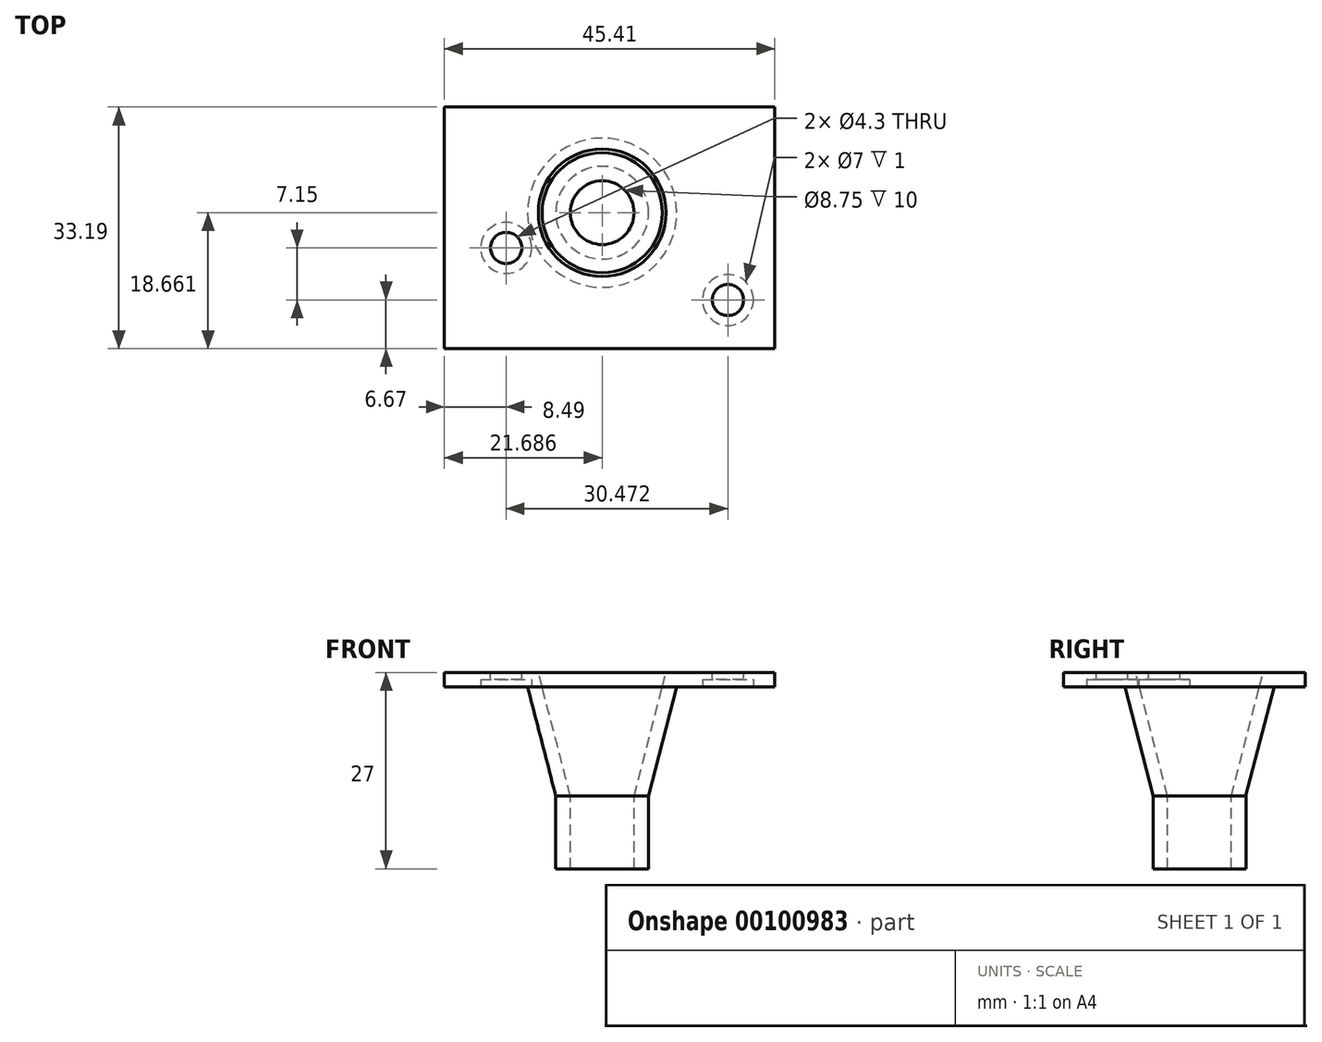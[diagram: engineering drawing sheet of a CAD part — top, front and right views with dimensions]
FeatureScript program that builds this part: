
annotation { "Feature Type Name" : "Feature", "Feature Type Description" : "" }
export const myFeature = defineFeature(function(context is Context, id is Id, definition is map)
    precondition{}
    {
        {
            var Q0;
            Q0=qCreatedBy(makeId("Top.planeOp"),FACE);
            var sketch = newSketch(context, id + "F0", { "sketchPlane" : qUnion([Q0])});
            skCircle(sketch, "E0", {"center": v(30.47, -7.15) * mm, "radius": 2.15 * mm});
            skCircle(sketch, "E1", {"center": v(0, 0) * mm, "radius": 2.15 * mm});
            skLineSegment(sketch, "E2.bottom", {"start": v(18.9, -0.85) * mm, "end": v(7.4, -0.85) * mm});
            skLineSegment(sketch, "E2.top", {"start": v(18.9, 10.65) * mm, "end": v(7.39, 10.65) * mm});
            skLineSegment(sketch, "E2.left", {"start": v(18.9, -0.85) * mm, "end": v(18.9, 10.65) * mm});
            skLineSegment(sketch, "E2.right", {"start": v(7.4, -0.85) * mm, "end": v(7.39, 10.65) * mm});
            skLineSegment(sketch, "E3.bottom", {"start": v(36.92, -13.82) * mm, "end": v(-8.49, -13.82) * mm});
            skLineSegment(sketch, "E3.top", {"start": v(36.92, 19.37) * mm, "end": v(-8.49, 19.37) * mm});
            skLineSegment(sketch, "E3.left", {"start": v(36.92, -13.82) * mm, "end": v(36.92, 19.37) * mm});
            skLineSegment(sketch, "E3.right", {"start": v(-8.49, -13.82) * mm, "end": v(-8.49, 19.37) * mm});
            skSolve(sketch);
        }
        {
            var Q0;
            Q0=makeQuery(id+"F0.imprint","IMPRINT",FACE,{"disambiguationData":[TD([[makeQuery(id+"F0.imprint","IMPRINT",EDGE,{"derivedFrom":sQuery(id+"F0.wireOp",EDGE,"E0")}),-1.0]])]});
            var Q1;
            Q1=makeQuery(id+"F0.imprint","IMPRINT",FACE,{"disambiguationData":[TD([[makeQuery(id+"F0.imprint","IMPRINT",EDGE,{"derivedFrom":sQuery(id+"F0.wireOp",EDGE,"E2.bottom")}),1.0]])]});
            extrude(context, id + "F1", {"entities" : qUnion([Q0, Q1]), "oppositeDirection" : true, "depth" : 2 * mm});
        }
        {
            var Q0;
            Q0=makeQuery(id+"F1.opExtrude","CAP_FACE",FACE,{"disambiguationData":[OSD([sQuery(id+"F0.wireOp",EDGE,"E0"),sQuery(id+"F0.wireOp",EDGE,"E1"),sQuery(id+"F0.wireOp",EDGE,"E2.bottom"),sQuery(id+"F0.wireOp",EDGE,"E2.top"),sQuery(id+"F0.wireOp",EDGE,"E2.left"),sQuery(id+"F0.wireOp",EDGE,"E2.right"),sQuery(id+"F0.wireOp",EDGE,"E3.bottom"),sQuery(id+"F0.wireOp",EDGE,"E3.top"),sQuery(id+"F0.wireOp",EDGE,"E3.left"),sQuery(id+"F0.wireOp",EDGE,"E3.right")])],"isStart":false});
            var sketch = newSketch(context, id + "F2", { "sketchPlane" : qUnion([Q0])});
            skCircle(sketch, "E4", {"center": v(0, 0) * mm, "radius": 3.5 * mm});
            skCircle(sketch, "E5", {"center": v(30.47, 7.15) * mm, "radius": 3.5 * mm});
            skSolve(sketch);
        }
        {
            var Q0;
            Q0=makeQuery(id+"F2.imprint","IMPRINT",FACE,{"disambiguationData":[TD([[makeQuery(id+"F2.imprint","IMPRINT",EDGE,{"derivedFrom":sQuery(id+"F2.wireOp",EDGE,"E5")}),1.0]])]});
            var Q1;
            Q1=makeQuery(id+"F2.imprint","IMPRINT",FACE,{"disambiguationData":[TD([[makeQuery(id+"F2.imprint","IMPRINT",EDGE,{"derivedFrom":sQuery(id+"F2.wireOp",EDGE,"E4")}),1.0]])]});
            extrude(context, id + "F3", {"entities" : qUnion([Q0, Q1]), "operationType" : NewBodyOperationType.REMOVE, "oppositeDirection" : true, "depth" : 1 * mm});
        }
        {
            var Q0;
            Q0=makeQuery(id+"F1.opExtrude","CAP_FACE",FACE,{"disambiguationData":[OSD([sQuery(id+"F0.wireOp",EDGE,"E0"),sQuery(id+"F0.wireOp",EDGE,"E1"),sQuery(id+"F0.wireOp",EDGE,"E2.bottom"),sQuery(id+"F0.wireOp",EDGE,"E2.top"),sQuery(id+"F0.wireOp",EDGE,"E2.left"),sQuery(id+"F0.wireOp",EDGE,"E2.right"),sQuery(id+"F0.wireOp",EDGE,"E3.bottom"),sQuery(id+"F0.wireOp",EDGE,"E3.top"),sQuery(id+"F0.wireOp",EDGE,"E3.left"),sQuery(id+"F0.wireOp",EDGE,"E3.right")])],"isStart":false});
            var sketch = newSketch(context, id + "F4", { "sketchPlane" : qUnion([Q0])});
            skCircle(sketch, "E6", {"center": v(13.2, -4.84) * mm, "radius": 8.25 * mm});
            skCircle(sketch, "E7", {"center": v(13.2, -4.84) * mm, "radius": 10.25 * mm});
            skSolve(sketch);
        }
        {
            var Q0;
            Q0=makeQuery(id+"F4.imprint","IMPRINT",FACE,{"disambiguationData":[TD([[makeQuery(id+"F4.imprint","IMPRINT",EDGE,{"derivedFrom":sQuery(id+"F4.wireOp",EDGE,"E7")}),-1.0]])]});
            var Q1;
            Q1 = qBodyType(qCreatedBy(id + "F6" ,EDGE), BodyType.WIRE);
            cPlane(context, id + "F5", {"entities" : qUnion([Q0, Q1]), "cplaneType" : CPlaneType.OFFSET, "offset" : 15 * mm, "width" : 150 * mm, "height" : 150 * mm});
        }
        {
            var Q0;
            Q0=qCreatedBy(id+"F5.planeOp",FACE);
            var sketch = newSketch(context, id + "F6", { "sketchPlane" : qUnion([Q0])});
            skCircle(sketch, "E8", {"center": v(13.2, -4.84) * mm, "radius": 6.37 * mm});
            skCircle(sketch, "E9", {"center": v(13.2, -4.84) * mm, "radius": 4.38 * mm});
            skSolve(sketch);
        }
        {
            var Q0;
            Q0=makeQuery(id+"F6.imprint","IMPRINT",FACE,{"disambiguationData":[TD([[makeQuery(id+"F6.imprint","IMPRINT",EDGE,{"derivedFrom":sQuery(id+"F6.wireOp",EDGE,"E8")}),1.0]])]});
            extrude(context, id + "F7", {"entities" : qUnion([Q0]), "depth" : 10 * mm});
        }
        {
            var Q0;
            Q0=makeQuery(id+"F4.imprint","IMPRINT",FACE,{"disambiguationData":[TD([[makeQuery(id+"F4.imprint","IMPRINT",EDGE,{"derivedFrom":makeQuery(id+"F1.opExtrude","CAP_EDGE",EDGE,{"disambiguationData":[OSD([sQuery(id+"F0.wireOp",EDGE,"E2.bottom")])],"isStart":false})}),1.0]])]});
            var Q1;
            Q1=makeQuery(id+"F4.imprint","IMPRINT",FACE,{"disambiguationData":[TD([[makeQuery(id+"F4.imprint","IMPRINT",EDGE,{"derivedFrom":sQuery(id+"F4.wireOp",EDGE,"E6")}),1.0]])]});
            var Q2;
            Q2=makeQuery(id+"F4.imprint","IMPRINT",FACE,{"disambiguationData":[TD([[makeQuery(id+"F4.imprint","IMPRINT",EDGE,{"derivedFrom":sQuery(id+"F4.wireOp",EDGE,"E6")}),-1.0]])]});
            extrude(context, id + "F8", {"entities" : qUnion([Q0, Q1, Q2]), "depth" : 15 * mm, "hasDraft" : true, "draftAngle" : 14.5 * degree, "draftPullDirection" : true});
        }
        {
            var Q0;
            Q0=makeQuery(id+"F6.imprint","IMPRINT",FACE,{"disambiguationData":[TD([[makeQuery(id+"F6.imprint","IMPRINT",EDGE,{"derivedFrom":sQuery(id+"F6.wireOp",EDGE,"E9")}),1.0]])]});
            var Q1;
            Q1=makeQuery(id+"F1.opExtrude","CAP_FACE",FACE,{"disambiguationData":[OSD([sQuery(id+"F0.wireOp",EDGE,"E0"),sQuery(id+"F0.wireOp",EDGE,"E1"),sQuery(id+"F0.wireOp",EDGE,"E2.bottom"),sQuery(id+"F0.wireOp",EDGE,"E2.top"),sQuery(id+"F0.wireOp",EDGE,"E2.left"),sQuery(id+"F0.wireOp",EDGE,"E2.right"),sQuery(id+"F0.wireOp",EDGE,"E3.bottom"),sQuery(id+"F0.wireOp",EDGE,"E3.top"),sQuery(id+"F0.wireOp",EDGE,"E3.left"),sQuery(id+"F0.wireOp",EDGE,"E3.right")])],"isStart":true});
            extrude(context, id + "F9", {"entities" : qUnion([Q0]), "operationType" : NewBodyOperationType.REMOVE, "endBound" : BoundingType.UP_TO_SURFACE, "oppositeDirection" : true, "endBoundEntityFace" : qUnion([Q1]), "depth" : 25 * mm, "hasDraft" : true, "draftAngle" : 14.5 * degree});
        }
    });
